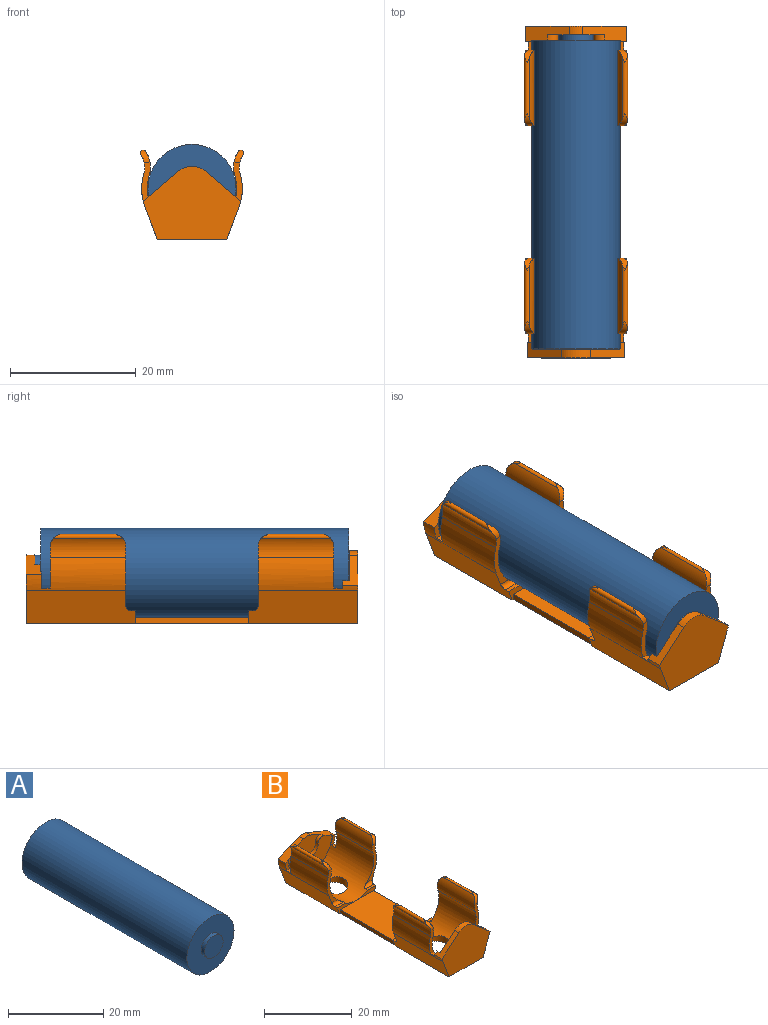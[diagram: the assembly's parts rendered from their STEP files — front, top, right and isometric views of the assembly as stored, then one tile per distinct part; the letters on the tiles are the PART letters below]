
ASSEMBLY  parts=2 mates=1
PART A: 7 faces, bbox 14x50x14 mm
  f0: cylinder r=7mm len=48.9mm, axis (0,-1,0), area 2150.7mm2, adj f2,f5
  f1: cylinder r=2.75mm len=5.5mm, axis (0,-1,0), area 17.3mm2, adj f2,f3
  f2: plane 14x14mm, normal (0,-1,0), area 130.2mm2, adj f0,f1
  f3: plane 5.5x5.5mm, normal (0,-1,0), area 23.8mm2, adj f1
  f4: cylinder r=3.5mm len=7mm, axis (0,1,0), area 2.2mm2, adj f5,f6
  f5: plane 14x14mm, normal (0,1,0), area 115.5mm2, adj f0,f4
  f6: plane 7x7mm, normal (0,1,0), area 38.5mm2, adj f4
PART B: 78 faces, bbox 16.5x52.8x14.3 mm
  f0: plane 6.25x2mm, normal (0,-1,0), area 4mm2, adj f2,f5,f29,f39,f76,f77
  f1: plane 6.25x2mm, normal (0,-1,0), area 3.8mm2, adj f2,f6,f33,f75,f77
  f2: cylinder r=7.1mm len=15.1mm, axis (0,1,0), area 324.3mm2, adj f0,f1,f4,f11,f12,f15,f17,f22
  f3: cylinder r=8mm len=15.85mm, axis (0,1,0), area 69.6mm2, adj f5,f7,f15,f18,f23,f25,f26,f28
  f4: plane 2.56x1.34mm, normal (0,-1,0), area 2.2mm2, adj f2,f8,f17,f30
  f5: plane 17.48x5.41mm, normal (-0.94,0,-0.35), area 92.9mm2, adj f0,f3,f18,f28,f29,f38,f39
  f6: plane 17.48x5.41mm, normal (0.94,0,-0.35), area 92.9mm2, adj f1,f8,f18,f33,f34,f37,f39
  f7: cylinder r=3.6mm len=12mm, axis (0,1,0), area 38.1mm2, adj f3,f13,f24,f25,f27,f28
  f8: cylinder r=8mm len=15.85mm, axis (0,1,0), area 69.6mm2, adj f4,f6,f9,f17,f18,f30,f31,f34
  f9: cylinder r=3.6mm len=12mm, axis (0,1,0), area 38.1mm2, adj f8,f10,f31,f32,f34,f35
  f10: cylinder r=0.45mm len=11.04mm, axis (0,1,0), area 13.4mm2, adj f9,f11,f32,f35
  f11: cylinder r=4.5mm len=12mm, axis (0,1,0), area 46.8mm2, adj f2,f10,f31,f32,f34,f35
  f12: cylinder r=4.5mm len=12mm, axis (0,1,0), area 46.8mm2, adj f2,f13,f24,f25,f27,f28
  f13: cylinder r=0.45mm len=11.04mm, axis (0,1,0), area 13.4mm2, adj f7,f12,f24,f27
  f14: plane 9.06x5.6mm, normal (0,-1,0), area 27.5mm2, adj f15,f16,f17,f19,f20,f21
  f15: plane 6.92x2.87mm, normal (-0.38,0,0.92), area 13.7mm2, adj f2,f3,f14,f16,f18,f19,f22,f23
  f16: cylinder r=2.8mm len=2.14mm, axis (0,-1,0), area 3mm2, adj f14,f15,f17,f18
  f17: plane 6.92x2.87mm, normal (0.38,0,0.92), area 13.7mm2, adj f2,f4,f8,f14,f16,f18,f21,f22
  f18: plane 15.99x10.9mm, normal (0,1,0), area 134.6mm2, adj f3,f5,f6,f8,f15,f16,f17,f39
  f19: cylinder r=1.25mm len=1.73mm, axis (0,1,0), area 2.2mm2, adj f14,f15,f20,f22
  f20: cylinder r=2.8mm len=5.6mm, axis (0,1,0), area 7.9mm2, adj f14,f19,f21,f22
  f21: cylinder r=1.25mm len=1.73mm, axis (0,1,0), area 2.2mm2, adj f14,f17,f20,f22
  f22: plane 14.2x8.35mm, normal (0,-1,0), area 73.7mm2, adj f2,f15,f17,f19,f20,f21
  f23: plane 2.56x1.34mm, normal (0,-1,0), area 2.2mm2, adj f2,f3,f15,f26
  f24: cylinder r=2mm len=2mm, axis (1,0,0), area 2.5mm2, adj f7,f12,f13,f25
  f25: plane 6.57x1.4mm, normal (0,1,0), area 6mm2, adj f2,f3,f7,f12,f24,f26
  f26: plane 1.4x0.95mm, normal (0,0,1), area 1.3mm2, adj f2,f3,f23,f25
  f27: cylinder r=2mm len=2mm, axis (1,0,0), area 2.5mm2, adj f7,f12,f13,f28
  f28: plane 9.4x3.28mm, normal (0,-1,0), area 9.5mm2, adj f2,f3,f5,f7,f12,f27,f38
  f29: plane 2.62x0.7mm, normal (0,0,1), area 1.8mm2, adj f0,f2,f5,f38
  f30: plane 1.4x0.95mm, normal (0,0,1), area 1.3mm2, adj f2,f4,f8,f31
  f31: plane 6.57x1.4mm, normal (0,1,0), area 6mm2, adj f2,f8,f9,f11,f30,f32
  f32: cylinder r=2mm len=2mm, axis (1,0,0), area 2.5mm2, adj f9,f10,f11,f31
  f33: plane 2.62x0.7mm, normal (0,0,1), area 1.8mm2, adj f1,f2,f6,f37
  f34: plane 9.4x3.28mm, normal (0,-1,0), area 9.5mm2, adj f2,f6,f8,f9,f11,f35,f37
  f35: cylinder r=2mm len=2mm, axis (1,0,0), area 2.5mm2, adj f9,f10,f11,f34
  f36: cylinder r=3.25mm len=6.5mm, axis (0,0,-1), area 28.3mm2, adj f2,f39
  f37: cylinder r=0.8mm len=2.92mm, axis (1,0,0), area 2.9mm2, adj f2,f6,f33,f34
  f38: cylinder r=0.8mm len=2.92mm, axis (1,0,0), area 2.9mm2, adj f2,f5,f28,f29
  f39: plane 52.7x11.01mm, normal (0,0,-1), area 509.2mm2, adj f0,f5,f6,f18,f36,f40,f70,f71
  f40: plane 6.25x2mm, normal (0,1,0), area 4mm2, adj f39,f68,f72,f73,f76,f77
  f41: cylinder r=2mm len=2mm, axis (1,0,0), area 2.5mm2, adj f42,f47,f51,f52
  f42: cylinder r=0.45mm len=11.04mm, axis (0,1,0), area 13.4mm2, adj f41,f45,f47,f52
  f43: cylinder r=0.45mm len=11.04mm, axis (0,1,0), area 13.4mm2, adj f44,f46,f48,f53
  f44: cylinder r=2mm len=2mm, axis (1,0,0), area 2.5mm2, adj f43,f48,f53,f54
  f45: cylinder r=2mm len=2mm, axis (1,0,0), area 2.5mm2, adj f42,f47,f52,f59
  f46: cylinder r=2mm len=2mm, axis (1,0,0), area 2.5mm2, adj f43,f48,f53,f60
  f47: cylinder r=3.6mm len=12mm, axis (0,1,0), area 38.1mm2, adj f41,f42,f45,f51,f59,f62
  f48: cylinder r=3.6mm len=12mm, axis (0,1,0), area 38.1mm2, adj f43,f44,f46,f54,f60,f66
  f49: plane 1.13x1.09mm, normal (0,1,0), area 0.7mm2, adj f50,f62,f63,f73
  f50: plane 1.4x0.95mm, normal (0,0,1), area 1.3mm2, adj f49,f51,f62,f73
  f51: plane 6.57x1.4mm, normal (0,-1,0), area 6mm2, adj f41,f47,f50,f52,f62,f73
  f52: cylinder r=4.5mm len=12mm, axis (0,1,0), area 46.8mm2, adj f41,f42,f45,f51,f59,f73
  f53: cylinder r=4.5mm len=12mm, axis (0,1,0), area 46.8mm2, adj f43,f44,f46,f54,f60,f73
  f54: plane 6.57x1.4mm, normal (0,-1,0), area 6mm2, adj f44,f48,f53,f55,f66,f73
  f55: plane 1.4x0.95mm, normal (0,0,1), area 1.3mm2, adj f54,f56,f66,f73
  f56: plane 1.13x1.09mm, normal (0,1,0), area 0.7mm2, adj f55,f65,f66,f73
  f57: plane 13.94x10.6mm, normal (0,1,0), area 99.9mm2, adj f63,f64,f65,f73
  f58: cylinder r=0.8mm len=2.92mm, axis (-1,0,0), area 2.9mm2, adj f59,f68,f72,f73
  f59: plane 9.4x3.28mm, normal (0,1,0), area 9.5mm2, adj f45,f47,f52,f58,f62,f72,f73
  f60: plane 9.4x3.28mm, normal (0,1,0), area 9.5mm2, adj f46,f48,f53,f61,f66,f71,f73
  f61: cylinder r=0.8mm len=2.92mm, axis (-1,0,0), area 2.9mm2, adj f60,f67,f71,f73
  f62: cylinder r=8mm len=15.85mm, axis (0,1,0), area 65.4mm2, adj f47,f49,f50,f51,f59,f63,f70,f72
  f63: plane 5.48x4.66mm, normal (-0.65,0,0.76), area 10.8mm2, adj f49,f57,f62,f64,f70,f73
  f64: cylinder r=3.5mm len=4.54mm, axis (0,1,0), area 6.7mm2, adj f57,f63,f65,f70
  f65: plane 5.48x4.66mm, normal (0.65,0,0.76), area 10.8mm2, adj f56,f57,f64,f66,f70,f73
  f66: cylinder r=8mm len=15.85mm, axis (0,1,0), area 65.4mm2, adj f48,f54,f55,f56,f60,f65,f70,f71
  f67: plane 2.62x0.7mm, normal (0,0,1), area 1.8mm2, adj f61,f69,f71,f73
  f68: plane 2.62x0.7mm, normal (0,0,1), area 1.8mm2, adj f40,f58,f72,f73
  f69: plane 6.25x2mm, normal (0,1,0), area 3.8mm2, adj f67,f71,f73,f75,f77
  f70: plane 15.49x11.6mm, normal (0,-1,0), area 130.4mm2, adj f39,f62,f63,f64,f65,f66,f71,f72
  f71: plane 17.48x5.41mm, normal (0.94,0,-0.35), area 92.9mm2, adj f39,f60,f61,f66,f67,f69,f70
  f72: plane 17.48x5.41mm, normal (-0.94,0,-0.35), area 92.9mm2, adj f39,f40,f58,f59,f62,f68,f70
  f73: cylinder r=7.1mm len=16mm, axis (0,1,0), area 341.4mm2, adj f40,f49,f50,f51,f52,f53,f54,f55
  f74: cylinder r=3.25mm len=6.5mm, axis (0,0,-1), area 28.3mm2, adj f39,f73
  f75: plane 18x1mm, normal (1,0,0), area 18mm2, adj f1,f39,f69,f77
  f76: plane 18x1mm, normal (-1,0,0), area 18mm2, adj f0,f39,f40,f77
  f77: plane 18x10.76mm, normal (0,0,1), area 193.7mm2, adj f0,f1,f40,f69,f75,f76
PLACE A rot(axis=(1,0,0),180deg) t=(0,25,0)mm
PLACE B at identity
MATE revolute A.f1 <-> B.f16  axis (0,1,0) through (0,25,0)mm
